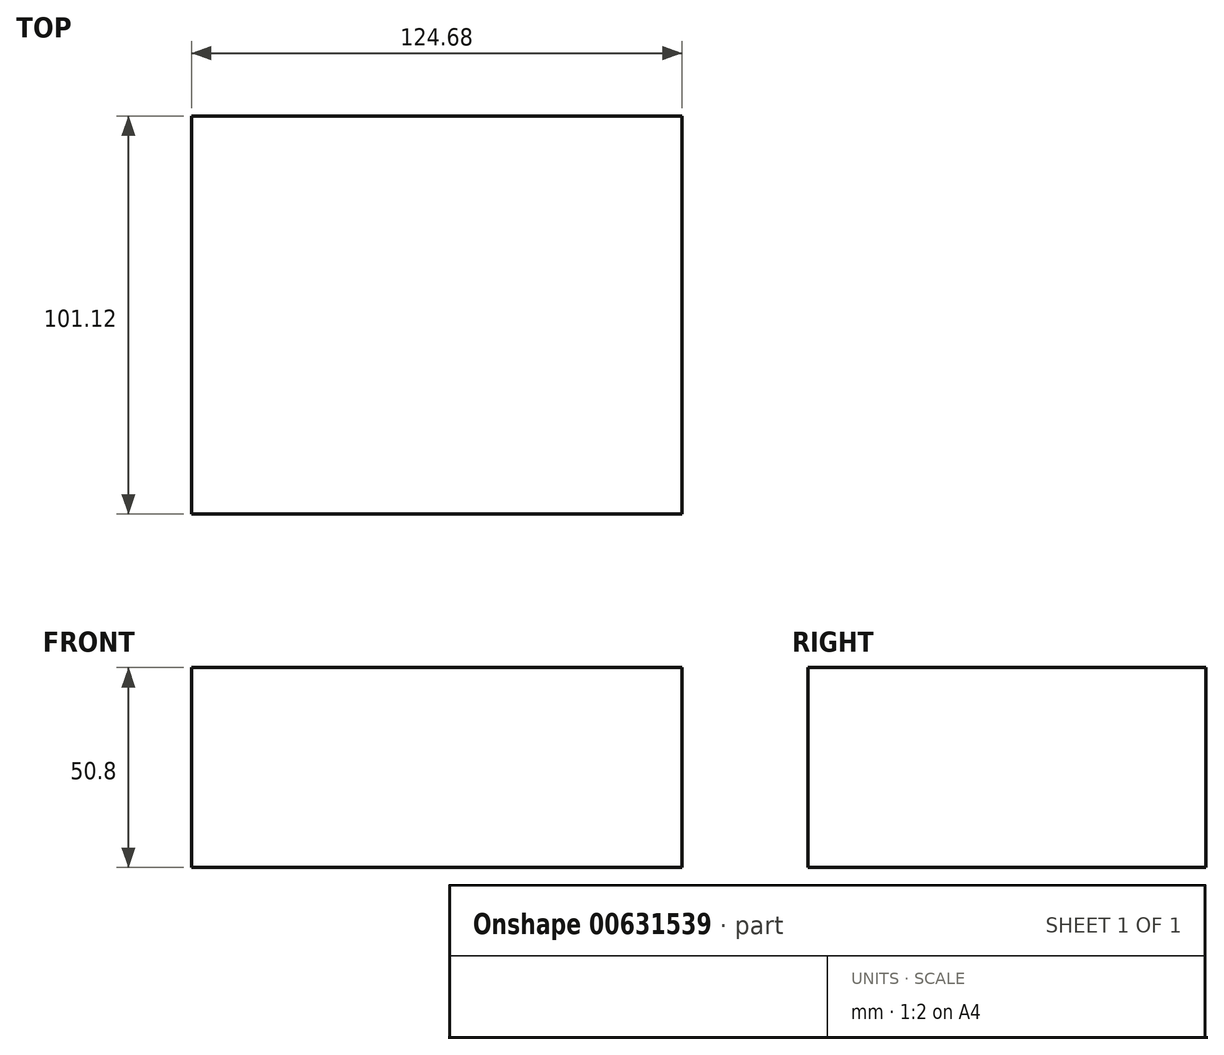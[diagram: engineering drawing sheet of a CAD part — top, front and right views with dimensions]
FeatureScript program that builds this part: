
annotation { "Feature Type Name" : "Feature", "Feature Type Description" : "" }
export const myFeature = defineFeature(function(context is Context, id is Id, definition is map)
    precondition{}
    {
        {
            var Q0;
            Q0=qCreatedBy(makeId("Top.planeOp"),FACE);
            var sketch = newSketch(context, id + "F0", { "sketchPlane" : qUnion([Q0])});
            skLineSegment(sketch, "E0.bottom", {"start": v(-59.73, 54.28) * mm, "end": v(64.95, 54.28) * mm});
            skLineSegment(sketch, "E0.top", {"start": v(-59.73, -46.84) * mm, "end": v(64.95, -46.84) * mm});
            skLineSegment(sketch, "E0.left", {"start": v(-59.73, 54.28) * mm, "end": v(-59.73, -46.84) * mm});
            skLineSegment(sketch, "E0.right", {"start": v(64.95, 54.28) * mm, "end": v(64.95, -46.84) * mm});
            skSolve(sketch);
        }
        {
            var Q0;
            Q0 = qSketchRegion(id + "F0", true);
            var Q1;
            Q1=sQuery(id+"F0.wireOp",EDGE,"E0.left");
            var Q2;
            Q2=sQuery(id+"F0.wireOp",EDGE,"E0.bottom");
            var Q3;
            Q3=sQuery(id+"F0.wireOp",EDGE,"E0.right");
            var Q4;
            Q4=sQuery(id+"F0.wireOp",EDGE,"E0.top");
            extrude(context, id + "F1", {"entities" : qUnion([Q0]), "bodyType" : ToolBodyType.SURFACE, "surfaceEntities" : qUnion([Q1, Q2, Q3, Q4]), "depth" : 50.8 * mm, "offsetDistance" : 25.4 * mm});
        }
    });
